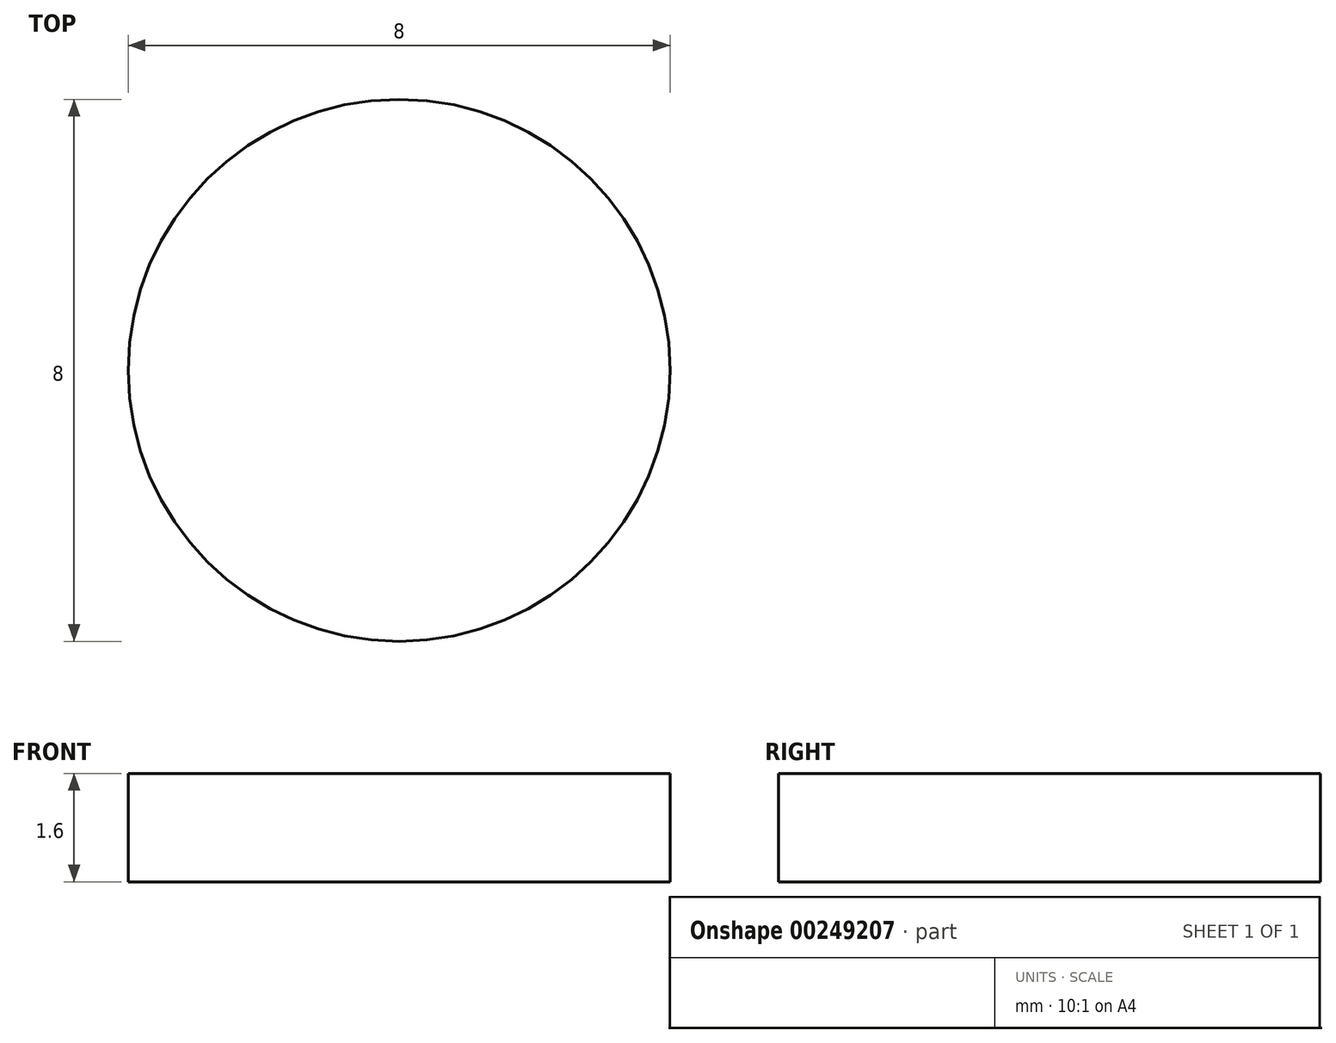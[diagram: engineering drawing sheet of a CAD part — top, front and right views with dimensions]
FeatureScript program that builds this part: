
annotation { "Feature Type Name" : "Feature", "Feature Type Description" : "" }
export const myFeature = defineFeature(function(context is Context, id is Id, definition is map)
    precondition{}
    {
        {
            var Q0;
            Q0=qCreatedBy(makeId("Top.planeOp"),FACE);
            var sketch = newSketch(context, id + "F0", { "sketchPlane" : qUnion([Q0])});
            skCircle(sketch, "E0", {"center": v(0, 0) * mm, "radius": 4 * mm});
            skSolve(sketch);
        }
        {
            var Q0;
            Q0 = qSketchRegion(id + "F0", true);
            extrude(context, id + "F1", {"entities" : qUnion([Q0]), "depth" : 1.6 * mm});
        }
    });
